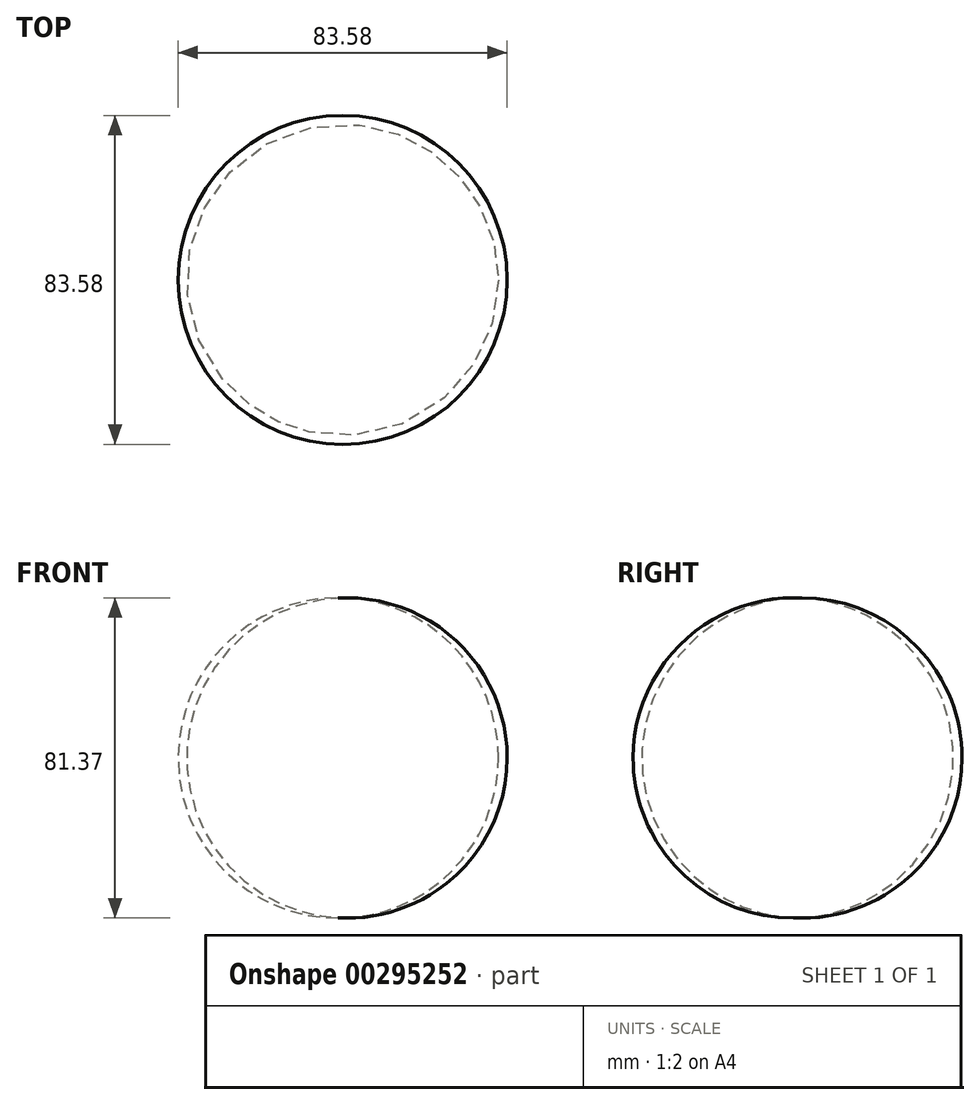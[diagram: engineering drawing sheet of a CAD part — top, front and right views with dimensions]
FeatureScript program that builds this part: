
annotation { "Feature Type Name" : "Feature", "Feature Type Description" : "" }
export const myFeature = defineFeature(function(context is Context, id is Id, definition is map)
    precondition{}
    {
        {
            var Q0;
            Q0=qCreatedBy(makeId("Front.planeOp"),FACE);
            var sketch = newSketch(context, id + "F0", { "sketchPlane" : qUnion([Q0])});
            skLineSegment(sketch, "E0", {"start": v(0, 76.45) * mm, "end": v(0, -76) * mm, "construction": true});
            skSolve(sketch);
        }
        {
            var Q0;
            Q0=qCreatedBy(makeId("Front.planeOp"),FACE);
            var sketch = newSketch(context, id + "F1", { "sketchPlane" : qUnion([Q0])});
            skArc(sketch, "E1", {"start": v(0, 48.23) * mm, "mid": v(-39.58, 7.56) * mm, "end": v(0, -33.12) * mm});
            skSolve(sketch);
        }
        {
            var Q0;
            Q0=sQuery(id+"F1.wireOp",EDGE,"E1");
            var Q1;
            Q1=sQuery(id+"F0.wireOp",EDGE,"E0");
            revolve(context, id + "F2", {"bodyType" : ToolBodyType.SURFACE, "surfaceEntities" : qUnion([Q0]), "axis" : qUnion([Q1]), "revolveType" : RevolveType.FULL});
        }
    });
